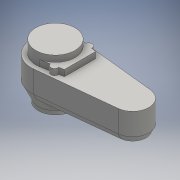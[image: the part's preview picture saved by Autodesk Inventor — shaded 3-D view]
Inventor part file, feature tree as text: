
AUTODESK INVENTOR PART (.ipt)
format: ipt  version: 2016 (Build 200138000, 138)  size: 175,104 bytes
history: native  units: mm
features: sketch x6, extrude x4, plane x2, loft x2, other x2, projected_geometry x1
ambient origin geometry x8: Origin, YZ Plane, XZ Plane, XY Plane, X Axis, Y Axis, Z Axis, Center Point
bodies: Solid1 (feature_tree)
feature tree (17):
  extrude  "Extrusion1"  Depth=20.292mm TaperAngle=0.0deg
  plane  "Work Plane1"
  loft  "Loft1"
  extrude  "Extrusion2"  TaperAngle=0.0deg  [1 undecoded]
  plane  "Work Plane2"
  loft  "Loft2"
  extrude  "Extrusion5"  Depth=31.0mm
  extrude  "Extrusion6"  Depth=34.5mm
  sketch  "Sketch1"  dims[d0=188.0mm d1=20.292mm d2=0.0mm]
  sketch  "Sketch2"  dims[d3=-105.0mm d4=267.0mm]
  other  "Edges1"
  sketch  "Sketch3"  dims[d5=0.0mm d6=90.0deg d7=0.0mm d8=90.0deg]
  projected_geometry  "Projected Loop1"
  sketch  "Sketch4"  dims[d9=178.0mm d10=425.0mm]
  other  "Edges2"
  sketch  "Sketch7"  dims[d11=121.0mm d12=0.0mm d13=31.0mm]
  sketch  "Sketch8"  dims[d14=149.088mm d15=238.088mm d16=0.0mm d17=90.0deg d18=0.0mm d19=90.0deg d30=216.0mm d31=171.724mm d32=135.0mm d33=40.0mm d34=89.0mm d35=34.5mm d36=0.0mm d37=34.5mm d38=0.0mm]
note: 1 required parameter value undecoded (feature->parameter linkage not recoverable at this tier; creation-order binding heuristic only, values carry confidence <= 0.55)
